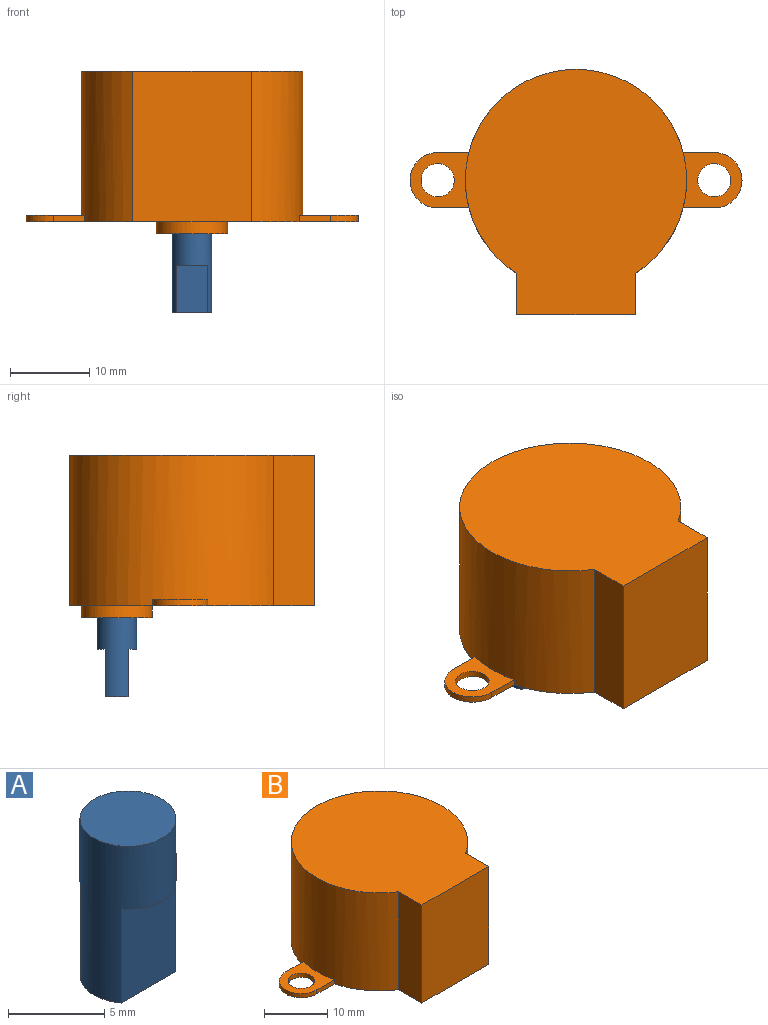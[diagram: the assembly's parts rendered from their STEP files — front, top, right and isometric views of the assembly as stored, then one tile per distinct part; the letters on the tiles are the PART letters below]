
ASSEMBLY  parts=2 mates=1
PART A: 7 faces, bbox 5x5x10 mm
  f0: plane 5x3mm, normal (0,0,-1), area 14mm2, adj f1,f3,f5
  f1: cylinder r=2.5mm len=10mm, axis (0,0,1), area 101.4mm2, adj f0,f2,f3,f4,f5,f6
  f2: plane 5x5mm, normal (0,0,1), area 19.6mm2, adj f1
  f3: plane 6x4mm, normal (0,1,0), area 24mm2, adj f0,f1,f4
  f4: plane 4x1mm, normal (0,0,-1), area 2.8mm2, adj f1,f3
  f5: plane 6x4mm, normal (0,-1,0), area 24mm2, adj f0,f1,f6
  f6: plane 4x1mm, normal (0,0,-1), area 2.8mm2, adj f1,f5
PART B: 20 faces, bbox 42x31x20.5 mm
  f0: cylinder r=14mm len=28mm, axis (0,0,-1), area 1359.2mm2, adj f2,f3,f4,f5,f6,f7,f10,f11
  f1: plane 19x15mm, normal (0,-1,0), area 285mm2, adj f2,f3,f4,f5
  f2: plane 19x5.18mm, normal (1,0,0), area 98.4mm2, adj f0,f1,f4,f5
  f3: plane 19x5.18mm, normal (-1,0,0), area 98.4mm2, adj f0,f1,f4,f5
  f4: plane 31x28mm, normal (0,0,1), area 671.3mm2, adj f0,f1,f2,f3
  f5: plane 42x31mm, normal (0,0,-1), area 669.5mm2, adj f0,f1,f2,f3,f6,f7,f8,f9
  f6: plane 3.94x0.8mm, normal (0,1,0), area 3.2mm2, adj f0,f5,f9,f10
  f7: plane 3.94x0.8mm, normal (0,-1,0), area 3.2mm2, adj f0,f5,f9,f10
  f8: cylinder r=2.1mm len=4.2mm, axis (0,0,-1), area 10.6mm2, adj f5,f10
  f9: cylinder r=3.5mm len=7mm, axis (0,0,-1), area 8.8mm2, adj f5,f6,f7,f10
  f10: plane 7.44x7mm, normal (0,0,1), area 30.9mm2, adj f0,f6,f7,f8,f9
  f11: plane 3.94x0.8mm, normal (0,-1,0), area 3.2mm2, adj f0,f5,f14,f15
  f12: plane 3.94x0.8mm, normal (0,1,0), area 3.2mm2, adj f0,f5,f14,f15
  f13: cylinder r=2.1mm len=4.2mm, axis (0,0,-1), area 10.6mm2, adj f5,f15
  f14: cylinder r=3.5mm len=7mm, axis (0,0,-1), area 8.8mm2, adj f5,f11,f12,f15
  f15: plane 7.44x7mm, normal (0,0,1), area 30.9mm2, adj f0,f11,f12,f13,f14
  f16: cylinder r=2.5mm len=5mm, axis (0,0,1), area 23.6mm2, adj f18,f19
  f17: cylinder r=4.5mm len=9mm, axis (0,0,1), area 42.4mm2, adj f5,f18
  f18: plane 9x9mm, normal (0,0,-1), area 44mm2, adj f16,f17
  f19: plane 5x5mm, normal (0,0,-1), area 19.6mm2, adj f16
PLACE A t=(2.77,-0.68,-2.53)mm
PLACE B t=(2.77,-0.68,-1.03)mm
MATE revolute A.f1 <-> B.f16  axis (0,0,1) through (2.77,7.32,-2.53)mm
